# Revit family: IS_Iom_A9128_BIM_NL
name_source: partatom
category: Plumbing Fixtures
revit_build: Autodesk Revit MEP 2016 (Build: 20161004_0715(x64)
units: mm (PartAtom-declared; Revit-internal decimal feet)

## family parameters
Always vertical = No
Cut with Voids When Loaded = No
OmniClass Number = 23.45.05.14.21.11
OmniClass Title = Bath/Shower Units
Part Type = Normal
Room Calculation Point = No
Round Connector Dimension = Use Diameter
Shared = No
Work Plane-Based = No

## types (1)
- A9128MY - IOM toilet brush, wall mounted, glass and stainless steel
    Accesoires = www.idealstandardnederland.nl
    Afmetingen = 0
    Afwerking = Staal geborsteld
    Artikelnummer = A9128MY
    Artikelomschrijving = ISI_IOM_ToiletBrushHolders_A9128MY
    Artikelreferentie = IOM toilet brush, wall mounted, glass and stainless steel
    Auteur = Ideal Standard
    BIMobject category = Accessories
    BOSUseNativeGeometries = 1
    Barcode = 4015413328098
    Beschrijvinggarantie = 4015413328098
    Brand url = www.idealstandardnederland.nl
    Breedte = 250
    BrutoGewicht = 0
    Cost = 0 $
    Description = IOM toilet brush, wall mounted, glass and stainless steel
    Diepte = 360 mm  [stored 1.1811 ft]
    EAN code = https://4015413328098
    Edition number = 1
    Eigenschappen = Closetborstelgarnituur (wandmontage). Inclusief bevestigingsset. Makkelijk schoon te maken, functioneel design. Closetborstelgarnituur en houder van metaal. Kunststof inzetstuk is uitneembaar voor eenvoudige reiniging. 2 geïntegreerde bevestigingspunten.
    Garantieonderdelen = 1
    Garantieunits = Jaar
    Hoogte = 120
    IFC Classification = Sanitary Terminal
    IfcExportAs = Ifc Sanitary Terminal Type
    Installatieinstructies = http://www.idealstandardnederland.nl
    Installation instructions = www.idealstandardnederland.nl
    Kleur = Staal geborsteld
    Lengte = 360 mm  [stored 1.1811 ft]
    Manufacturer = www.idealstandardnederland.nl
    Manufacturer name = Ideal Standard
    Materiaal = Messing
    Merk = Ideal Standard
    Model = A9128MY
    NBS Reference Code = 35-75-86
    NBS Reference Description = Toilet Brush Holders
    Nettogewicht = 0
    Nominal height = 402
    Nominal width = 90
    NominalHeight = 401 mm
    NominalLength = 113 mm
    NominalWidth = 90 mm  [stored 0.295276 ft]
    OmniClass Code = 23-31 25 00
    OmniClass Description = Toilet and Bath Specialties
    Product Guid = 568f3a2b-783a-4186-b127-52550e4b6f32
    Product SKU = A9128
    Product data url = https://bimobject.com
    Product family = IOM
    Product group = Accessories
    Product name = IOM toilet brush, wall mounted, glass and stainless steel
    QR code = http://bimobject.com
    Revisie = 1
    Size = 401 x 113 x 90mm
    Technical description = www.idealstandardnederland.nl
    Telefoonnummer = 31 (0) 77 355 08 08
    Typeconnectie = Sanitair
    URL = www.idealstandardnederland.nl
    Uniclass 1.4 Code = L7313
    Uniclass 1.4 Description = Sanitary above ground pipes and fittings
    Uniclass 2.0 Code = PR-35-75-86
    Uniclass 2.0 Description = Toilet Brush Holders
    Uniclass 2015 Code = Pr_40_20_76_86
    Uniclass 2015 Name = Toilet brush holders
    Uniclass2015Beschrijving = Toilet brush holders
    Uniclass2015Referentie = Pr_40_20_76_86
    Uniclass2015Version = Products v1.1
    Versie = 1
    Vervangingskosten = 0
    Volumeunits = Liter
    Weight Net (Kg) = 0.89

note: [stored X ft] marks values corroborated as IEEE doubles in the binary element streams (Revit-internal decimal feet)

## geometry (parser evidence)
native form markers: Blend x2, Sweep x3
no freeform markers — native parametric forms only
